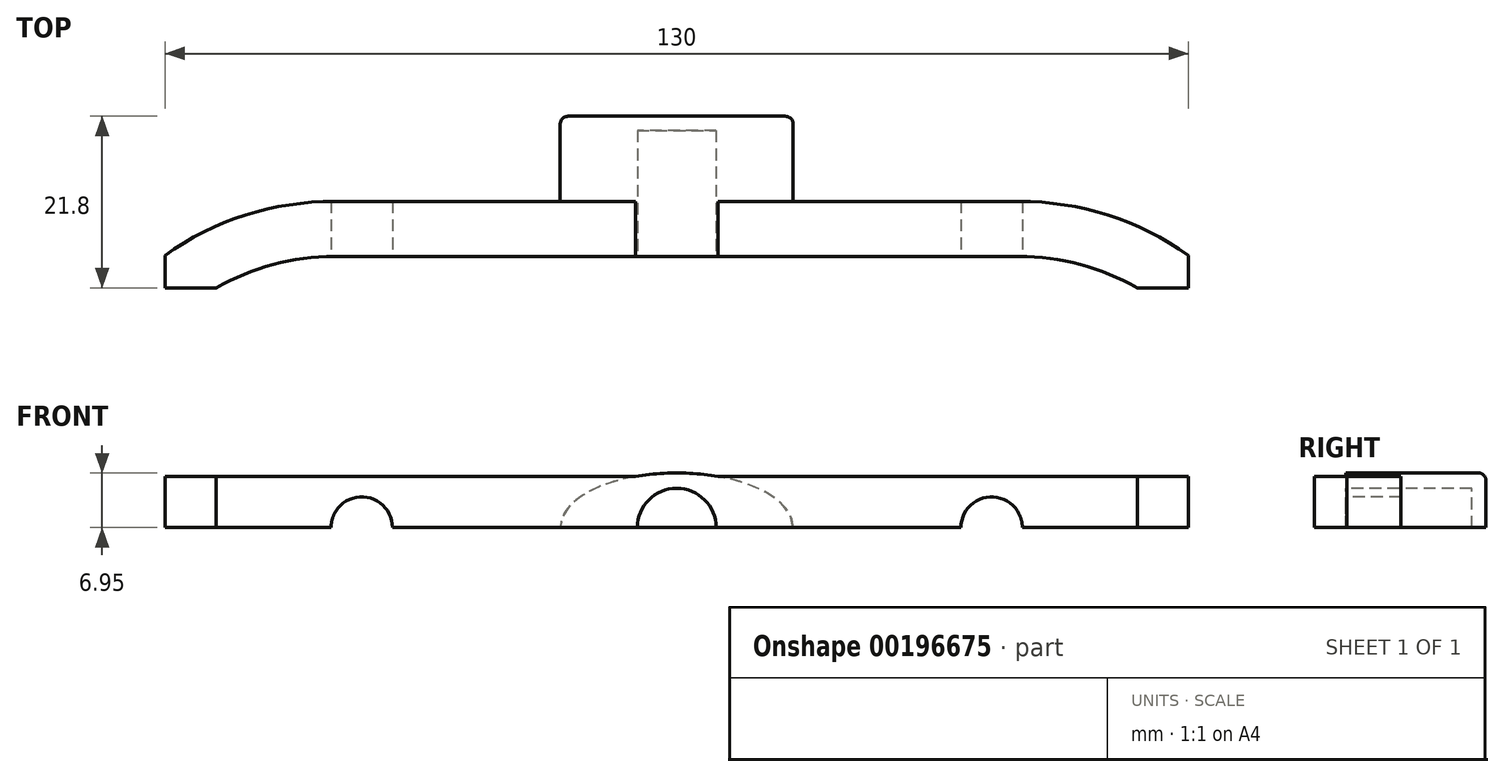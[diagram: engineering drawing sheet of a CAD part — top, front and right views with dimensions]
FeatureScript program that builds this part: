
annotation { "Feature Type Name" : "Feature", "Feature Type Description" : "" }
export const myFeature = defineFeature(function(context is Context, id is Id, definition is map)
    precondition{}
    {
        {
            var Q0;
            Q0=qCreatedBy(makeId("Top.planeOp"),FACE);
            var sketch = newSketch(context, id + "F0", { "sketchPlane" : qUnion([Q0])});
            skLineSegment(sketch, "E0", {"start": v(0, 7) * mm, "end": v(43.5, 7) * mm});
            skArc(sketch, "E1", {"start": v(65, 0.14) * mm, "mid": v(54.78, 5.24) * mm, "end": v(43.5, 7) * mm});
            skLineSegment(sketch, "E2", {"start": v(65, 0.14) * mm, "end": v(65, -4) * mm});
            skLineSegment(sketch, "E3", {"start": v(58.5, -4) * mm, "end": v(65, -4) * mm});
            skArc(sketch, "E4", {"start": v(58.5, -4) * mm, "mid": v(51.26, -1.02) * mm, "end": v(43.5, 0) * mm});
            skLineSegment(sketch, "E5", {"start": v(43.5, 0) * mm, "end": v(0, 0) * mm});
            skLineSegment(sketch, "E6.MirrorCS", {"start": v(0, 7) * mm, "end": v(-43.5, 7) * mm});
            skArc(sketch, "E7.MirrorCS", {"start": v(-65, 0.14) * mm, "mid": v(-54.78, 5.24) * mm, "end": v(-43.5, 7) * mm});
            skLineSegment(sketch, "E8.MirrorCS", {"start": v(-65, 0.14) * mm, "end": v(-65, -4) * mm});
            skLineSegment(sketch, "E9.MirrorCS", {"start": v(-58.5, -4) * mm, "end": v(-65, -4) * mm});
            skArc(sketch, "E10.MirrorCS", {"start": v(-58.5, -4) * mm, "mid": v(-51.26, -1.02) * mm, "end": v(-43.5, 0) * mm});
            skLineSegment(sketch, "E11.MirrorCS", {"start": v(-43.5, 0) * mm, "end": v(0, 0) * mm});
            skSolve(sketch);
        }
        {
            var Q0;
            Q0=qCreatedBy(makeId("Front.planeOp"),FACE);
            var sketch = newSketch(context, id + "F1", { "sketchPlane" : qUnion([Q0])});
            skCircle(sketch, "E12", {"center": v(-40, 0) * mm, "radius": 3.9 * mm});
            skCircle(sketch, "E13", {"center": v(40, 0) * mm, "radius": 3.9 * mm});
            skCircle(sketch, "E14", {"center": v(0, 0) * mm, "radius": 5 * mm});
            skEllipse(sketch, "E15", {"center": v(0, 0) * mm, "majorRadius": 14.8 * mm, "minorRadius": 6.95 * mm, "majorAxis": v(1, 0)});
            skLineSegment(sketch, "E16", {"start": v(-14.8, 0) * mm, "end": v(14.8, 0) * mm});
            skSolve(sketch);
        }
        {
            var Q0;
            {var subQ1=sQuery(id+"F0.wireOp",EDGE,"4XtGPDmJ-u0uF-y0Cj-QDHr-XvjftfuhsU4g");Q0=makeQuery(id+"F0.imprint","IMPRINT",FACE,{"disambiguationData":[TD([[makeQuery(id+"F0.imprint","IMPRINT",EDGE,{"derivedFrom":subQ1}),1.0]])]});}
            var Q1;
            Q1=makeQuery(id+"F0.imprint","IMPRINT",FACE,{"disambiguationData":[TD([[makeQuery(id+"F0.imprint","IMPRINT",EDGE,{"derivedFrom":sQuery(id+"F0.wireOp",EDGE,"E0")}),-1.0]])]});
            extrude(context, id + "F2", {"entities" : qUnion([Q0, Q1]), "depth" : 6.5 * mm});
        }
        {
            var Q0;
            {var subQ0=sQuery(id+"F1.wireOp",EDGE,"E16");var subQ1=sQuery(id+"F1.wireOp",EDGE,"E14");var subQ2=makeQuery(id+"F1.imprint","INTERSECT",VERTEX,{"disambiguationData":[OD(0.0)],"derivedFrom":[subQ1,subQ0]});Q0=makeQuery(id+"F1.imprint","IMPRINT",FACE,{"disambiguationData":[TD([[makeQuery(id+"F1.imprint","IMPRINT",EDGE,{"disambiguationData":[TD([[subQ2,1.0]])],"derivedFrom":subQ1}),-1.0]])]});}
            var Q1;
            {var subQ0=sQuery(id+"F1.wireOp",EDGE,"E16");var subQ1=sQuery(id+"F1.wireOp",EDGE,"E14");var subQ2=makeQuery(id+"F1.imprint","INTERSECT",VERTEX,{"disambiguationData":[OD(0.0)],"derivedFrom":[subQ1,subQ0]});Q1=makeQuery(id+"F1.imprint","IMPRINT",FACE,{"disambiguationData":[TD([[makeQuery(id+"F1.imprint","IMPRINT",EDGE,{"disambiguationData":[TD([[subQ2,1.0]])],"derivedFrom":subQ1}),1.0]])]});}
            extrude(context, id + "F3", {"entities" : qUnion([Q0, Q1]), "operationType" : NewBodyOperationType.ADD, "oppositeDirection" : true, "depth" : 17.8 * mm});
        }
        {
            var Q0;
            Q0=makeQuery(id+"F1.imprint","IMPRINT",FACE,{"disambiguationData":[TD([[makeQuery(id+"F1.imprint","IMPRINT",EDGE,{"derivedFrom":sQuery(id+"F1.wireOp",EDGE,"E12")}),1.0]])]});
            var Q1;
            Q1=makeQuery(id+"F1.imprint","IMPRINT",FACE,{"disambiguationData":[TD([[makeQuery(id+"F1.imprint","IMPRINT",EDGE,{"derivedFrom":sQuery(id+"F1.wireOp",EDGE,"E13")}),1.0]])]});
            var Q2;
            {var subQ0=sQuery(id+"F1.wireOp",EDGE,"E16");var subQ1=sQuery(id+"F1.wireOp",EDGE,"E14");var subQ2=makeQuery(id+"F1.imprint","INTERSECT",VERTEX,{"disambiguationData":[OD(0.0)],"derivedFrom":[subQ1,subQ0]});Q2=makeQuery(id+"F1.imprint","IMPRINT",FACE,{"disambiguationData":[TD([[makeQuery(id+"F1.imprint","IMPRINT",EDGE,{"disambiguationData":[TD([[subQ2,1.0]])],"derivedFrom":subQ1}),1.0]])]});}
            var Q3;
            {var subQ0=sQuery(id+"F1.wireOp",EDGE,"E16");var subQ1=sQuery(id+"F1.wireOp",EDGE,"E14");var subQ2=makeQuery(id+"F1.imprint","INTERSECT",VERTEX,{"disambiguationData":[OD(0.0)],"derivedFrom":[subQ1,subQ0]});Q3=makeQuery(id+"F1.imprint","IMPRINT",FACE,{"disambiguationData":[TD([[makeQuery(id+"F1.imprint","IMPRINT",EDGE,{"disambiguationData":[TD([[subQ2,-1.0]])],"derivedFrom":subQ1}),1.0]])]});}
            extrude(context, id + "F4", {"entities" : qUnion([Q0, Q1, Q2, Q3]), "operationType" : NewBodyOperationType.REMOVE, "oppositeDirection" : true, "depth" : 16 * mm});
        }
        {
            var Q0;
            Q0=makeQuery(id+"F3.opExtrude","CAP_EDGE",EDGE,{"disambiguationData":[OSD([sQuery(id+"F1.wireOp",EDGE,"E15")])],"isStart":false});
            fillet(context, id + "F5", {"entities" : qUnion([Q0]), "radius" : 1 * mm, "tangentPropagation" : true, "allowEdgeOverflow" : false});
        }
    });
